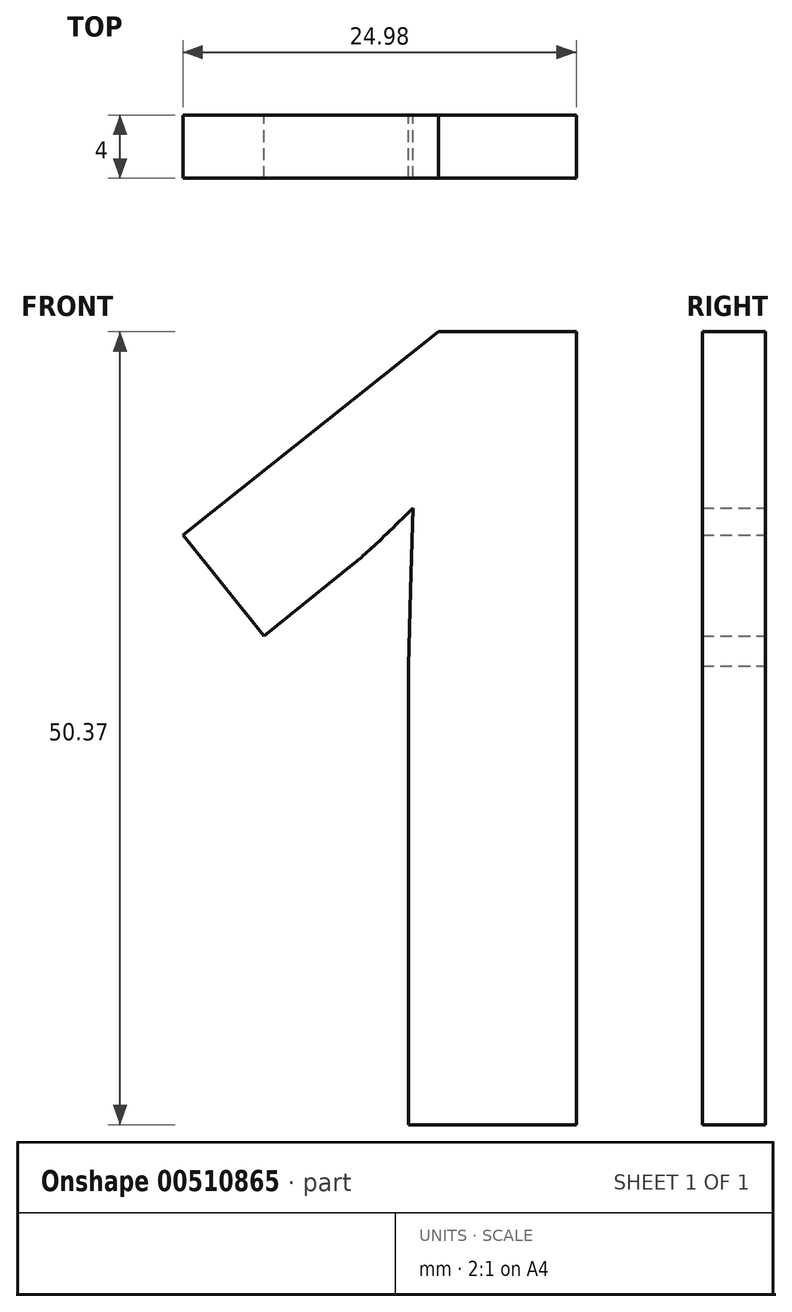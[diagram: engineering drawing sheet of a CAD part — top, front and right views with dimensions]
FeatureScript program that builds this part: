
annotation { "Feature Type Name" : "Feature", "Feature Type Description" : "" }
export const myFeature = defineFeature(function(context is Context, id is Id, definition is map)
    precondition{}
    {
        {
            var Q0;
            Q0=qCreatedBy(makeId("Front.planeOp"),FACE);
            var sketch = newSketch(context, id + "F0", { "sketchPlane" : qUnion([Q0])});
            skText(sketch, "E0", { "text": "1", "fontName": "OpenSans-Bold.ttf"});
            const initialGuessF0  = {"E0": [0, 0, 1, 0, 0.0508]};
            skSetInitialGuess(sketch, initialGuessF0);
            skSolve(sketch);
        }
        {
            var Q0;
            Q0=makeQuery(id+"F0.imprint","IMPRINT",FACE,{"disambiguationData":[TD([[makeQuery(id+"F0.imprint","IMPRINT",EDGE,{"derivedFrom":sQuery(id+"F0.wireOp",EDGE,"E0.sketch_text.stroke-0")}),-1.0]])]});
            extrude(context, id + "F1", {"entities" : qUnion([Q0]), "depth" : 4 * mm});
        }
    });
